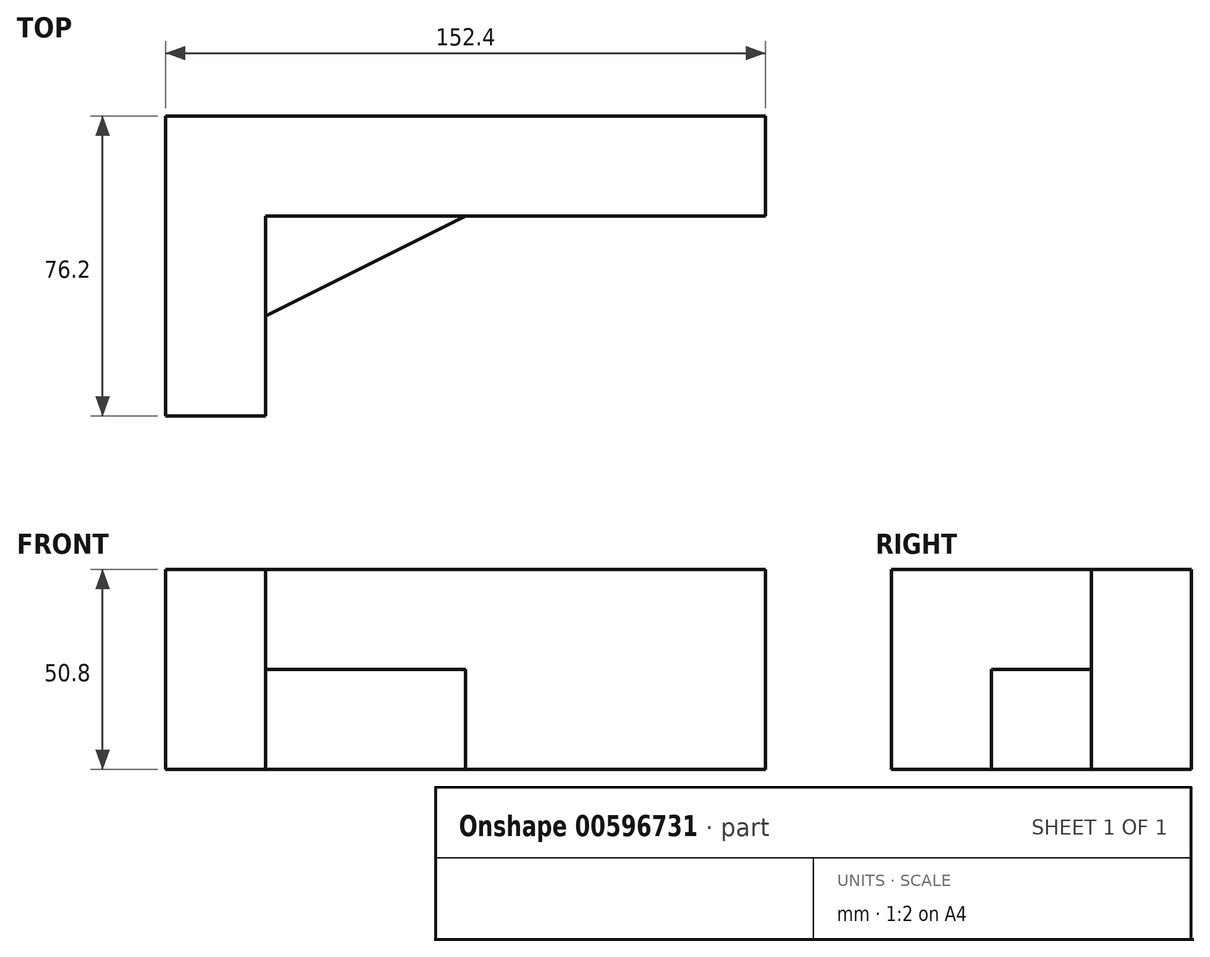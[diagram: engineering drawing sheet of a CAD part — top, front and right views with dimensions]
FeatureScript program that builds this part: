
annotation { "Feature Type Name" : "Feature", "Feature Type Description" : "" }
export const myFeature = defineFeature(function(context is Context, id is Id, definition is map)
    precondition{}
    {
        {
            var Q0;
            Q0=qCreatedBy(makeId("Top.planeOp"),FACE);
            var sketch = newSketch(context, id + "F0", { "sketchPlane" : qUnion([Q0])});
            skLineSegment(sketch, "E0", {"start": v(0, 0) * mm, "end": v(0, 76.2) * mm});
            skLineSegment(sketch, "E1", {"start": v(0, 76.2) * mm, "end": v(152.4, 76.2) * mm});
            skLineSegment(sketch, "E2", {"start": v(152.4, 76.2) * mm, "end": v(152.4, 50.8) * mm});
            skLineSegment(sketch, "E3", {"start": v(152.4, 50.8) * mm, "end": v(25.4, 50.8) * mm});
            skLineSegment(sketch, "E4", {"start": v(25.4, 50.8) * mm, "end": v(25.4, 0) * mm});
            skLineSegment(sketch, "E5", {"start": v(25.4, 0) * mm, "end": v(0, 0) * mm});
            skLineSegment(sketch, "E6", {"start": v(25.4, 25.4) * mm, "end": v(76.2, 50.8) * mm});
            skLineSegment(sketch, "E7", {"start": v(25.4, 25.4) * mm, "end": v(25.4, 50.8) * mm});
            skLineSegment(sketch, "E8", {"start": v(25.4, 50.8) * mm, "end": v(76.2, 50.8) * mm});
            skSolve(sketch);
        }
        {
            var Q0;
            Q0=makeQuery(id+"F0.imprint","IMPRINT",FACE,{"disambiguationData":[TD([[makeQuery(id+"F0.imprint","IMPRINT",EDGE,{"derivedFrom":sQuery(id+"F0.wireOp",EDGE,"E0")}),-1.0]])]});
            extrude(context, id + "F1", {"entities" : qUnion([Q0]), "depth" : 50.8 * mm, "offsetDistance" : 25.4 * mm});
        }
        {
            var Q0;
            Q0 = qSketchRegion(id + "F0", true);
            extrude(context, id + "F2", {"entities" : qUnion([Q0]), "operationType" : NewBodyOperationType.ADD, "depth" : 25.4 * mm, "offsetDistance" : 25.4 * mm});
        }
    });
